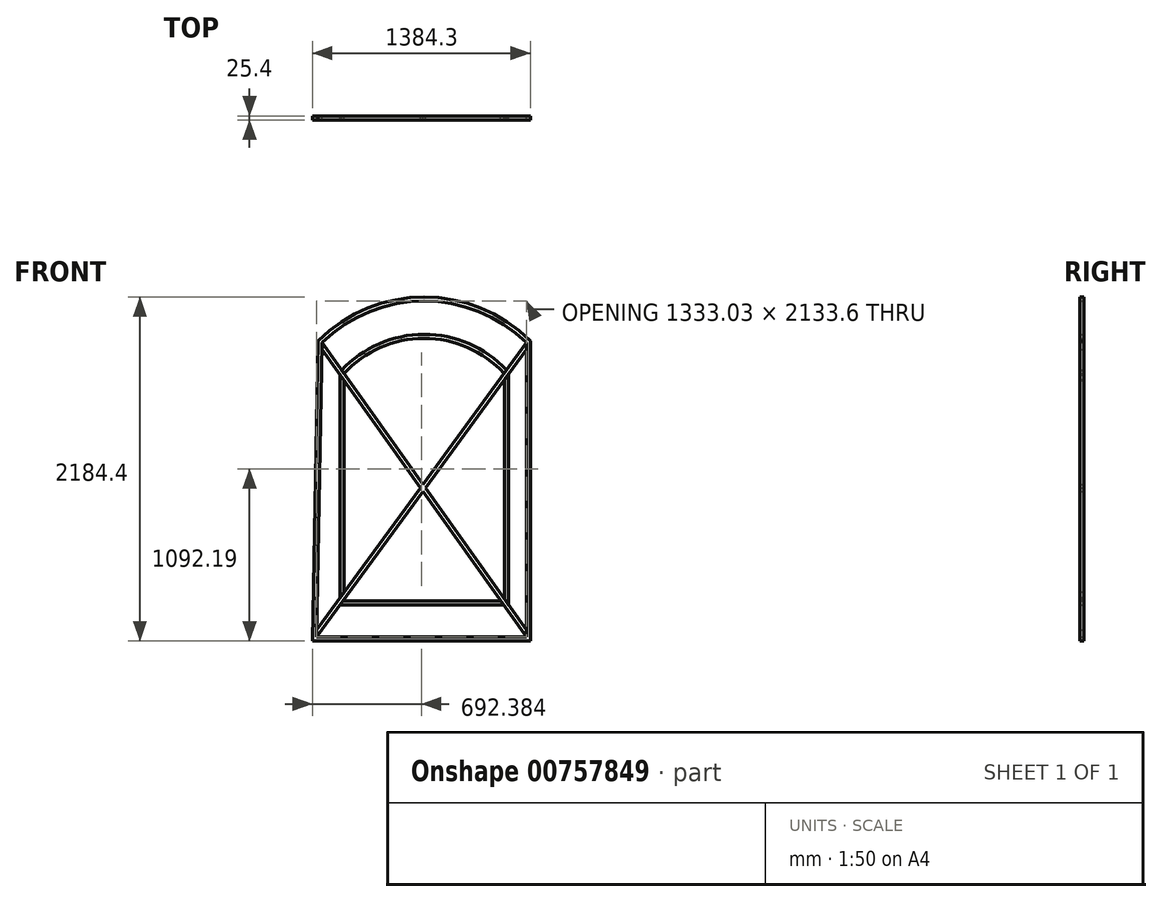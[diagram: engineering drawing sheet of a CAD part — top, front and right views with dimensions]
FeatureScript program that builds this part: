
annotation { "Feature Type Name" : "Feature", "Feature Type Description" : "" }
export const myFeature = defineFeature(function(context is Context, id is Id, definition is map)
    precondition{}
    {
        {
            var Q0;
            Q0=qCreatedBy(makeId("Front.planeOp"),FACE);
            var sketch = newSketch(context, id + "F0", { "sketchPlane" : qUnion([Q0])});
            skLineSegment(sketch, "E0.bottom", {"start": v(-934.83, 228.82) * mm, "end": v(414.55, 228.82) * mm});
            skLineSegment(sketch, "E0.top", {"start": v(-934.83, 2133.82) * mm, "end": v(414.55, 2133.82) * mm, "construction": true});
            skLineSegment(sketch, "E0.left", {"start": v(-934.83, 228.82) * mm, "end": v(-934.83, 2133.82) * mm, "construction": true});
            skLineSegment(sketch, "E0.right", {"start": v(414.55, 228.82) * mm, "end": v(414.55, 2133.82) * mm});
            skArc(sketch, "E1", {"start": v(414.55, 2133.82) * mm, "mid": v(-260.14, 2413.22) * mm, "end": v(-934.83, 2133.82) * mm});
            skLineSegment(sketch, "E2.0", {"start": v(-909.43, 254.22) * mm, "end": v(-909.43, 2123.2) * mm, "construction": true});
            skLineSegment(sketch, "E2.1", {"start": v(-909.43, 254.22) * mm, "end": v(389.15, 254.22) * mm});
            skLineSegment(sketch, "E2.2", {"start": v(389.15, 254.22) * mm, "end": v(389.15, 2123.2) * mm});
            skArc(sketch, "E2.3", {"start": v(389.15, 2123.2) * mm, "mid": v(-260.14, 2387.82) * mm, "end": v(-909.43, 2123.2) * mm});
            skLineSegment(sketch, "E3.0", {"start": v(-795.13, 368.52) * mm, "end": v(-795.13, 1936.65) * mm});
            skLineSegment(sketch, "E3.1", {"start": v(-795.13, 368.52) * mm, "end": v(274.85, 368.52) * mm, "construction": true});
            skLineSegment(sketch, "E3.2", {"start": v(274.85, 368.52) * mm, "end": v(274.85, 1936.65) * mm});
            skLineSegment(sketch, "E4.0", {"start": v(-782.43, 381.22) * mm, "end": v(-782.43, 2133.82) * mm, "construction": true});
            skLineSegment(sketch, "E4.1", {"start": v(-782.43, 381.22) * mm, "end": v(262.15, 381.22) * mm, "construction": true});
            skLineSegment(sketch, "E4.2", {"start": v(262.15, 381.22) * mm, "end": v(262.15, 2133.82) * mm, "construction": true});
            skLineSegment(sketch, "E5.0", {"start": v(-769.73, 393.92) * mm, "end": v(-769.73, 1926.86) * mm});
            skLineSegment(sketch, "E5.1", {"start": v(-769.73, 393.92) * mm, "end": v(249.45, 393.92) * mm, "construction": true});
            skLineSegment(sketch, "E5.2", {"start": v(249.45, 393.92) * mm, "end": v(249.45, 1926.86) * mm});
            skArc(sketch, "E6", {"start": v(274.85, 1936.65) * mm, "mid": v(-260.14, 2176.16) * mm, "end": v(-795.13, 1936.65) * mm});
            skLineSegment(sketch, "E7", {"start": v(-260.14, 2413.22) * mm, "end": v(-260.14, 2176.16) * mm, "construction": true});
            skLineSegment(sketch, "E8", {"start": v(-124.96, 2403.6) * mm, "end": v(-158.54, 2168.92) * mm, "construction": true});
            skLineSegment(sketch, "E9", {"start": v(-361.74, 2168.92) * mm, "end": v(-395.32, 2403.6) * mm, "construction": true});
            skLineSegment(sketch, "E10", {"start": v(-395.32, 2403.6) * mm, "end": v(-260.14, 2422.94) * mm, "construction": true});
            skLineSegment(sketch, "E11", {"start": v(-124.96, 2403.6) * mm, "end": v(-260.14, 2422.94) * mm, "construction": true});
            skPoint(sketch, "E12", {"position": v(-260.14, 2436.92) * mm});
            skLineSegment(sketch, "E13", {"start": v(-361.74, 2168.92) * mm, "end": v(-260.14, 2168.92) * mm, "construction": true});
            skLineSegment(sketch, "E14", {"start": v(-260.14, 2168.92) * mm, "end": v(-158.54, 2168.92) * mm, "construction": true});
            skArc(sketch, "E15", {"start": v(249.45, 1926.86) * mm, "mid": v(-260.14, 2150.76) * mm, "end": v(-769.73, 1926.86) * mm});
            skLineSegment(sketch, "E16", {"start": v(-361.74, 2168.92) * mm, "end": v(-358.14, 2143.78) * mm, "construction": true});
            skLineSegment(sketch, "E17", {"start": v(-158.54, 2168.92) * mm, "end": v(-162.14, 2143.78) * mm, "construction": true});
            skLineSegment(sketch, "E18", {"start": v(-260.14, 2150.76) * mm, "end": v(-260.14, 2176.16) * mm, "construction": true});
            skPoint(sketch, "E18.startSnap0", {"position": v(-260.14, 2150.76) * mm});
            skLineSegment(sketch, "E19", {"start": v(-769.73, 1926.86) * mm, "end": v(-795.13, 1926.86) * mm, "construction": true});
            skLineSegment(sketch, "E20", {"start": v(-943.88, 254.22) * mm, "end": v(389.15, 2080.13) * mm, "construction": true});
            skLineSegment(sketch, "E21", {"start": v(-943.07, 298.4) * mm, "end": v(389.15, 2123.2) * mm, "construction": true});
            skLineSegment(sketch, "E22", {"start": v(-248, 1207.4) * mm, "end": v(-268.5, 1222.38) * mm, "construction": true});
            skLineSegment(sketch, "E23", {"start": v(-289.2, 1207.66) * mm, "end": v(-268.5, 1222.38) * mm, "construction": true});
            skLineSegment(sketch, "E24", {"start": v(389.15, 254.22) * mm, "end": v(-909.43, 2079.4) * mm, "construction": true});
            skLineSegment(sketch, "E25", {"start": v(-909.43, 2123.2) * mm, "end": v(389.15, 298.03) * mm, "construction": true});
            skLineSegment(sketch, "E26", {"start": v(-769.73, 484.08) * mm, "end": v(-769.73, 393.92) * mm});
            skLineSegment(sketch, "E27", {"start": v(-769.73, 484.08) * mm, "end": v(249.45, 484.08) * mm});
            skLineSegment(sketch, "E28", {"start": v(249.45, 393.92) * mm, "end": v(249.45, 484.08) * mm});
            skLineSegment(sketch, "E29", {"start": v(274.85, 458.68) * mm, "end": v(274.85, 368.52) * mm});
            skLineSegment(sketch, "E30", {"start": v(274.85, 458.68) * mm, "end": v(-795.13, 458.68) * mm});
            skLineSegment(sketch, "E31", {"start": v(-795.13, 368.52) * mm, "end": v(-795.13, 458.68) * mm});
            skLineSegment(sketch, "E32", {"start": v(-769.73, 484.08) * mm, "end": v(-769.73, 458.68) * mm, "construction": true});
            skLineSegment(sketch, "E33", {"start": v(-943.88, 254.22) * mm, "end": v(-909.43, 2123.2) * mm});
            skLineSegment(sketch, "E34", {"start": v(-934.83, 2133.82) * mm, "end": v(-969.75, 228.82) * mm});
            skLineSegment(sketch, "E35", {"start": v(-943.88, 254.22) * mm, "end": v(-969.28, 254.68) * mm, "construction": true});
            skLineSegment(sketch, "E36", {"start": v(-934.83, 228.82) * mm, "end": v(-969.75, 228.82) * mm});
            skLineSegment(sketch, "E37", {"start": v(-943.88, 254.22) * mm, "end": v(-909.43, 254.22) * mm});
            skSolve(sketch);
        }
        {
            var Q0;
            Q0 = qSketchRegion(id + "F0", true);
            var Q1;
            Q1=makeQuery(id+"F0.imprint","IMPRINT",FACE,{"disambiguationData":[TD([[makeQuery(id+"F0.imprint","IMPRINT",EDGE,{"derivedFrom":sQuery(id+"F0.wireOp",EDGE,"E3.0")}),-1.0]])]});
            var Q2;
            {var subQ0=sQuery(id+"F0.wireOp",EDGE,"E27");Q2=makeQuery(id+"F0.imprint","IMPRINT",FACE,{"disambiguationData":[TD([[makeQuery(id+"F0.imprint","IMPRINT",EDGE,{"derivedFrom":subQ0}),-1.0]])]});}
            extrude(context, id + "F1", {"entities" : qUnion([Q0, Q1, Q2]), "depth" : 25.4 * mm, "offsetDistance" : 25.4 * mm});
        }
        {
            var Q0;
            Q0=qCreatedBy(makeId("Front.planeOp"),FACE);
            var sketch = newSketch(context, id + "F2", { "sketchPlane" : qUnion([Q0])});
            skLineSegment(sketch, "E38", {"start": v(-943.88, 254.22) * mm, "end": v(389.15, 2080.13) * mm});
            skLineSegment(sketch, "E39", {"start": v(389.15, 2080.13) * mm, "end": v(389.15, 2123.2) * mm});
            skLineSegment(sketch, "E40", {"start": v(389.15, 2123.2) * mm, "end": v(-943.07, 298.4) * mm});
            skLineSegment(sketch, "E41", {"start": v(-943.07, 298.4) * mm, "end": v(-943.88, 254.22) * mm});
            skLineSegment(sketch, "E42", {"start": v(389.15, 298.03) * mm, "end": v(-909.43, 2123.2) * mm});
            skLineSegment(sketch, "E43", {"start": v(-909.43, 2123.2) * mm, "end": v(-909.43, 2079.4) * mm});
            skLineSegment(sketch, "E44", {"start": v(-909.43, 2079.4) * mm, "end": v(389.15, 254.22) * mm});
            skLineSegment(sketch, "E45", {"start": v(389.15, 254.22) * mm, "end": v(389.15, 298.03) * mm});
            skLineSegment(sketch, "E46", {"start": v(-943.88, 254.22) * mm, "end": v(-1004.41, 298.4) * mm, "construction": true});
            skLineSegment(sketch, "E47", {"start": v(-1004.41, 298.4) * mm, "end": v(349.13, 2152.42) * mm, "construction": true});
            skLineSegment(sketch, "E48", {"start": v(389.15, 2123.2) * mm, "end": v(349.13, 2152.42) * mm, "construction": true});
            skSolve(sketch);
        }
        {
            var Q0;
            Q0 = qSketchRegion(id + "F2", true);
            extrude(context, id + "F3", {"entities" : qUnion([Q0]), "depth" : 25.4 * mm, "offsetDistance" : 25.4 * mm});
        }
        {
            var Q0;
            Q0=makeQuery(id+"F3.opExtrude","SWEPT_BODY",BODY,{"disambiguationData":[OSD([sQuery(id+"F2.wireOp",EDGE,"E38"),sQuery(id+"F2.wireOp",EDGE,"E39"),sQuery(id+"F2.wireOp",EDGE,"E40"),sQuery(id+"F2.wireOp",EDGE,"E41"),sQuery(id+"F2.wireOp",EDGE,"E42"),sQuery(id+"F2.wireOp",EDGE,"E43"),sQuery(id+"F2.wireOp",EDGE,"E44"),sQuery(id+"F2.wireOp",EDGE,"E45")])]});
            var Q1;
            Q1=makeQuery(id+"F1.opExtrude","SWEPT_BODY",BODY,{"disambiguationData":[OSD([sQuery(id+"F0.wireOp",EDGE,"E3.0"),sQuery(id+"F0.wireOp",EDGE,"E3.2"),sQuery(id+"F0.wireOp",EDGE,"E5.0"),sQuery(id+"F0.wireOp",EDGE,"E5.2"),sQuery(id+"F0.wireOp",EDGE,"E6"),sQuery(id+"F0.wireOp",EDGE,"E15"),sQuery(id+"F0.wireOp",EDGE,"E27"),sQuery(id+"F0.wireOp",EDGE,"E30")])]});
            booleanBodies(context, id + "F4", {"operationType" : BooleanOperationType.SUBTRACTION, "tools" : qUnion([Q0]), "targets" : qUnion([Q1]), "keepTools" : true});
        }
    });
